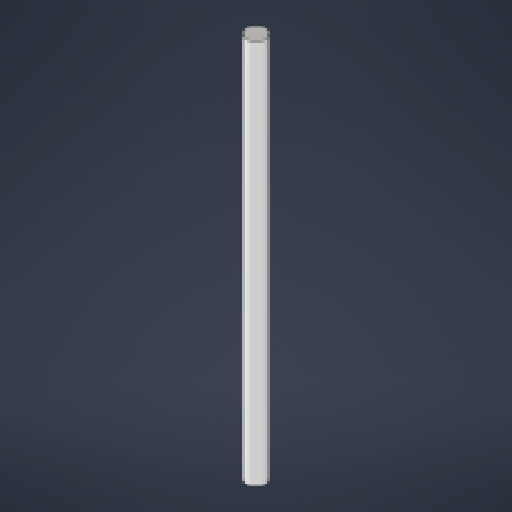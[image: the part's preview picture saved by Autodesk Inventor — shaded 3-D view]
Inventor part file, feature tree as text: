
AUTODESK INVENTOR PART (.ipt)
format: ipt  version: 2023.2 (Build 272271000, 271)  size: 118,784 bytes
history: native  units: mm
features: extrude x1, sketch x1
ambient origin geometry x8: Origin, YZ Plane, XZ Plane, XY Plane, X Axis, Y Axis, Z Axis, Center Point
bodies: Volumenkörper1 (feature_tree)
feature tree (2):
  extrude  "Extrusion1"  Depth=150.0mm TaperAngle=0.0deg
  sketch  "Skizze1"  dims[d0=6.0mm d1=150.0mm d2=0.0mm]
